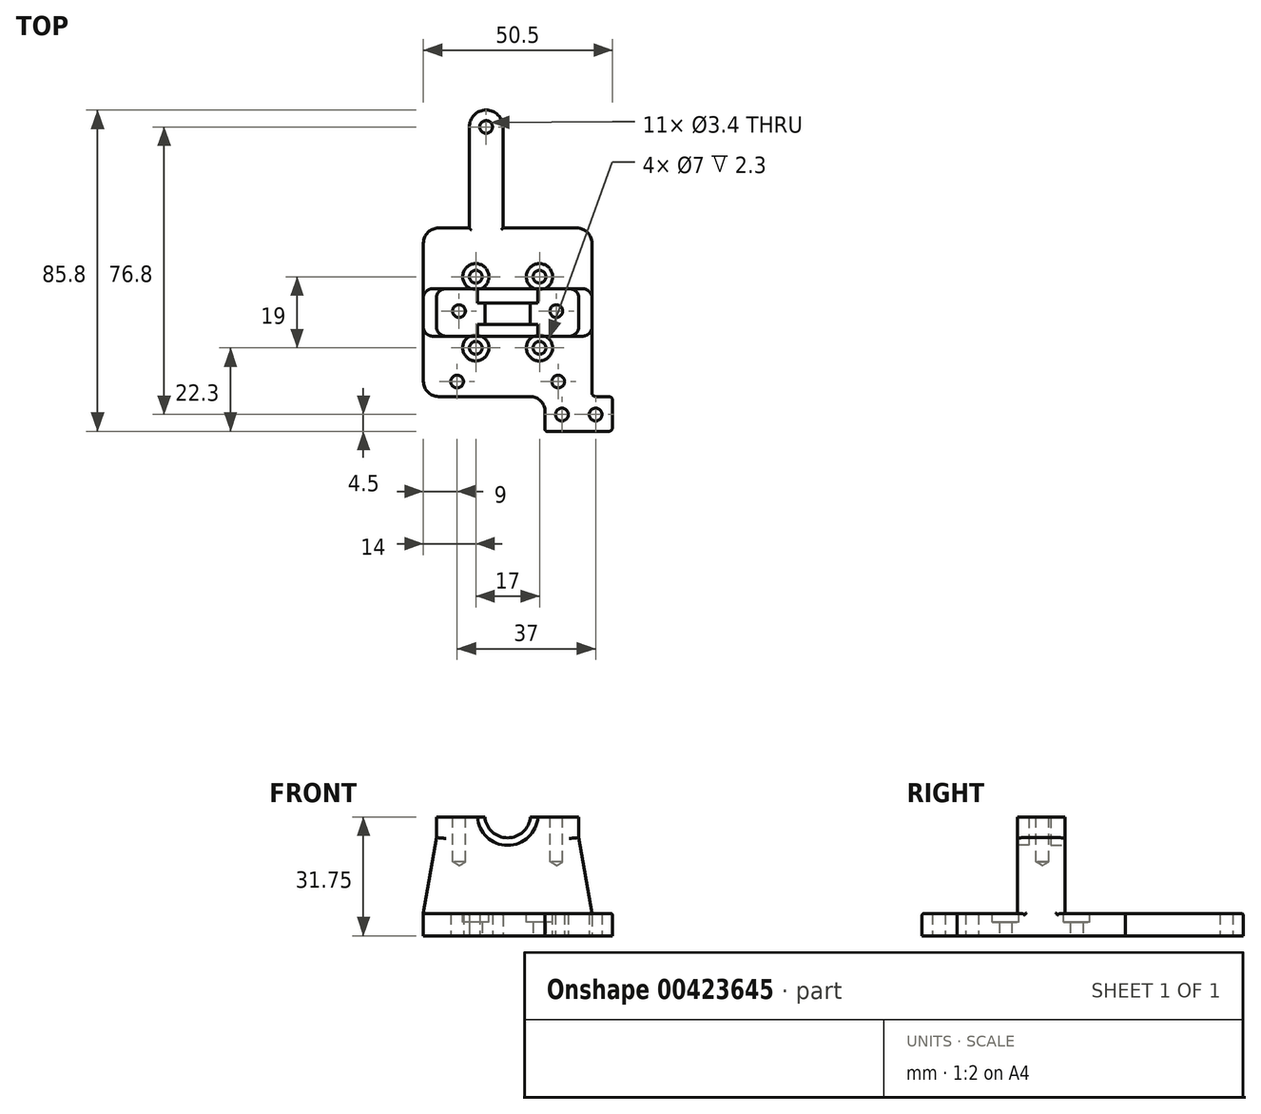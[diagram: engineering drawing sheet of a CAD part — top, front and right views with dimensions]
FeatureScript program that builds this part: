
annotation { "Feature Type Name" : "Feature", "Feature Type Description" : "" }
export const myFeature = defineFeature(function(context is Context, id is Id, definition is map)
    precondition{}
    {
        {
            var Q0;
            Q0=qCreatedBy(makeId("Top.planeOp"),FACE);
            cPlane(context, id + "F0", {"entities" : qUnion([Q0]), "cplaneType" : CPlaneType.OFFSET, "offset" : 16 * mm, "oppositeDirection" : true, "width" : 150 * mm, "height" : 150 * mm});
        }
        {
            var Q0;
            Q0=qCreatedBy(id+"F0.planeOp",FACE);
            var sketch = newSketch(context, id + "F1", { "sketchPlane" : qUnion([Q0])});
            skLineSegment(sketch, "E0.bottom", {"start": v(-22.5, -29.62) * mm, "end": v(-22.5, 7.38) * mm});
            skLineSegment(sketch, "E0.top", {"start": v(22.5, -32.62) * mm, "end": v(22.5, 7.38) * mm});
            skLineSegment(sketch, "E0.left", {"start": v(-18.5, -33.62) * mm, "end": v(6, -33.62) * mm});
            skLineSegment(sketch, "E0.right", {"start": v(-18.5, 11.38) * mm, "end": v(18.5, 11.38) * mm});
            skPoint(sketch, "E1.visualSharp", {"position": v(22.5, -33.62) * mm});
            skPoint(sketch, "E2.visualSharp", {"position": v(22.5, 11.38) * mm});
            skArc(sketch, "E2.filletArc", {"start": v(22.5, 7.38) * mm, "mid": v(21.33, 10.2) * mm, "end": v(18.5, 11.38) * mm});
            skPoint(sketch, "E3.visualSharp", {"position": v(-22.5, 11.38) * mm});
            skArc(sketch, "E3.filletArc", {"start": v(-18.5, 11.38) * mm, "mid": v(-21.33, 10.2) * mm, "end": v(-22.5, 7.38) * mm});
            skPoint(sketch, "E4.visualSharp", {"position": v(-22.5, -33.62) * mm});
            skArc(sketch, "E4.filletArc", {"start": v(-22.5, -29.62) * mm, "mid": v(-21.33, -32.45) * mm, "end": v(-18.5, -33.62) * mm});
            skLineSegment(sketch, "E5.top", {"start": v(22, -42.92) * mm, "end": v(10.5, -42.92) * mm});
            skLineSegment(sketch, "E5.right", {"start": v(10, -37.62) * mm, "end": v(10, -42.42) * mm});
            skPoint(sketch, "E6.visualSharp", {"position": v(10, -42.92) * mm});
            skArc(sketch, "E6.filletArc", {"start": v(10, -42.42) * mm, "mid": v(10.15, -42.77) * mm, "end": v(10.5, -42.92) * mm});
            skPoint(sketch, "E7.visualSharp", {"position": v(22.5, -42.92) * mm});
            skCircle(sketch, "E8", {"center": v(13.5, -29.62) * mm, "radius": 1.7 * mm});
            skPoint(sketch, "E8.first.point", {"position": v(11.95, -30.32) * mm});
            skPoint(sketch, "E8.second.point", {"position": v(15.02, -28.87) * mm});
            skPoint(sketch, "E8.third.point", {"position": v(14.54, -30.97) * mm});
            skLineSegment(sketch, "E9", {"start": v(10, -33.62) * mm, "end": v(22.5, -33.62) * mm, "construction": true});
            skCircle(sketch, "E10.MirrorC", {"center": v(14.5, -38.42) * mm, "radius": 1.7 * mm});
            skLineSegment(sketch, "E11", {"start": v(0, -37.3) * mm, "end": v(0, 46.97) * mm, "construction": true});
            skCircle(sketch, "E12.MirrorC", {"center": v(-13.5, -29.62) * mm, "radius": 1.7 * mm});
            skLineSegment(sketch, "E13", {"start": v(-41.46, -11.12) * mm, "end": v(34.1, -11.12) * mm, "construction": true});
            skCircle(sketch, "E14", {"center": v(-8.5, -20.62) * mm, "radius": 1.7 * mm});
            skCircle(sketch, "E15.MirrorC", {"center": v(8.5, -20.62) * mm, "radius": 1.7 * mm});
            skCircle(sketch, "E16.MirrorC", {"center": v(-8.5, -1.62) * mm, "radius": 1.7 * mm});
            skCircle(sketch, "E17.MirrorC", {"center": v(8.5, -1.62) * mm, "radius": 1.7 * mm});
            skLineSegment(sketch, "E18.bottom", {"start": v(-10.25, 11.38) * mm, "end": v(-1.25, 11.38) * mm});
            skLineSegment(sketch, "E18.left", {"start": v(-10.25, 11.38) * mm, "end": v(-10.25, 38.38) * mm});
            skLineSegment(sketch, "E18.right", {"start": v(-1.25, 11.38) * mm, "end": v(-1.25, 38.38) * mm});
            skArc(sketch, "E19", {"start": v(-10.25, 38.38) * mm, "mid": v(-5.75, 42.88) * mm, "end": v(-1.25, 38.38) * mm});
            skCircle(sketch, "E20", {"center": v(-5.75, 38.38) * mm, "radius": 1.7 * mm});
            skPoint(sketch, "E21.visualSharp", {"position": v(10, -33.62) * mm});
            skArc(sketch, "E21.filletArc", {"start": v(10, -37.62) * mm, "mid": v(8.83, -34.8) * mm, "end": v(6, -33.62) * mm});
            skLineSegment(sketch, "E22", {"start": v(10.13, -20.12) * mm, "end": v(10.13, -52.89) * mm, "construction": true});
            skLineSegment(sketch, "E23", {"start": v(17.44, -42.92) * mm, "end": v(27, -42.92) * mm});
            skLineSegment(sketch, "E24", {"start": v(28, -41.92) * mm, "end": v(28, -34.62) * mm});
            skLineSegment(sketch, "E25", {"start": v(27, -33.62) * mm, "end": v(23.5, -33.62) * mm});
            skPoint(sketch, "E26.visualSharp", {"position": v(28, -42.92) * mm});
            skArc(sketch, "E26.filletArc", {"start": v(27, -42.92) * mm, "mid": v(27.7, -42.63) * mm, "end": v(28, -41.92) * mm});
            skPoint(sketch, "E27.visualSharp", {"position": v(28, -33.62) * mm});
            skArc(sketch, "E27.filletArc", {"start": v(28, -34.62) * mm, "mid": v(27.7, -33.91) * mm, "end": v(27, -33.62) * mm});
            skArc(sketch, "E28.filletArc", {"start": v(22.5, -32.62) * mm, "mid": v(22.8, -33.33) * mm, "end": v(23.5, -33.62) * mm});
            skLineSegment(sketch, "E29", {"start": v(19, -42.92) * mm, "end": v(19, -32.16) * mm, "construction": true});
            skCircle(sketch, "E30.MirrorC", {"center": v(23.5, -38.42) * mm, "radius": 1.7 * mm});
            skLineSegment(sketch, "E31", {"start": v(14.5, -34.27) * mm, "end": v(14.5, -44.4) * mm, "construction": true});
            skSolve(sketch);
        }
        {
            var Q0;
            Q0=qSketchRegion(id+"F1",true);
            extrude(context, id + "F2", {"entities" : qUnion([Q0]), "depth" : 6 * mm});
        }
        {
            var Q0;
            Q0=makeQuery(id+"F2.opExtrude","CAP_FACE",FACE,{"disambiguationData":[OSD([sQuery(id+"F1.wireOp",EDGE,"E0.bottom"),sQuery(id+"F1.wireOp",EDGE,"E0.top"),sQuery(id+"F1.wireOp",EDGE,"E0.left"),sQuery(id+"F1.wireOp",EDGE,"E0.right"),sQuery(id+"F1.wireOp",EDGE,"E2.filletArc"),sQuery(id+"F1.wireOp",EDGE,"E3.filletArc"),sQuery(id+"F1.wireOp",EDGE,"E4.filletArc"),sQuery(id+"F1.wireOp",EDGE,"E5.top"),sQuery(id+"F1.wireOp",EDGE,"E5.left"),sQuery(id+"F1.wireOp",EDGE,"E5.right"),sQuery(id+"F1.wireOp",EDGE,"E6.filletArc"),sQuery(id+"F1.wireOp",EDGE,"E7.filletArc"),sQuery(id+"F1.wireOp",EDGE,"E8"),sQuery(id+"F1.wireOp",EDGE,"E10.MirrorC"),sQuery(id+"F1.wireOp",EDGE,"E12.MirrorC"),sQuery(id+"F1.wireOp",EDGE,"1abc18dc-51f7-492f-8969-0957bb5dfce40.MirrorC"),sQuery(id+"F1.wireOp",EDGE,"E14"),sQuery(id+"F1.wireOp",EDGE,"E15.MirrorC"),sQuery(id+"F1.wireOp",EDGE,"E16.MirrorC"),sQuery(id+"F1.wireOp",EDGE,"E17.MirrorC"),sQuery(id+"F1.wireOp",EDGE,"E18.left"),sQuery(id+"F1.wireOp",EDGE,"E18.right"),sQuery(id+"F1.wireOp",EDGE,"E19"),sQuery(id+"F1.wireOp",EDGE,"E20")])],"isStart":false});
            var sketch = newSketch(context, id + "F3", { "sketchPlane" : qUnion([Q0])});
            skPoint(sketch, "E32.0", {"position": v(-8.5, -1.62) * mm});
            skPoint(sketch, "E33.0", {"position": v(8.5, -1.62) * mm});
            skPoint(sketch, "E34.0", {"position": v(-8.5, -20.62) * mm});
            skPoint(sketch, "E35.0", {"position": v(8.5, -20.62) * mm});
            skSolve(sketch);
        }
        {
            var Q0;
            Q0=sQuery(id+"F3.wireOp",VERTEX,"E32.0");
            var Q1;
            Q1=sQuery(id+"F3.wireOp",VERTEX,"E33.0");
            var Q2;
            Q2=sQuery(id+"F3.wireOp",VERTEX,"E34.0");
            var Q3;
            Q3=sQuery(id+"F3.wireOp",VERTEX,"E35.0");
            var Q4;
            Q4=makeQuery(id+"F2.opExtrude","SWEPT_BODY",BODY,{"disambiguationData":[OSD([sQuery(id+"F1.wireOp",EDGE,"E0.bottom"),sQuery(id+"F1.wireOp",EDGE,"E0.top"),sQuery(id+"F1.wireOp",EDGE,"E0.left"),sQuery(id+"F1.wireOp",EDGE,"E0.right"),sQuery(id+"F1.wireOp",EDGE,"E2.filletArc"),sQuery(id+"F1.wireOp",EDGE,"E3.filletArc"),sQuery(id+"F1.wireOp",EDGE,"E4.filletArc"),sQuery(id+"F1.wireOp",EDGE,"E5.top"),sQuery(id+"F1.wireOp",EDGE,"E5.left"),sQuery(id+"F1.wireOp",EDGE,"E5.right"),sQuery(id+"F1.wireOp",EDGE,"E6.filletArc"),sQuery(id+"F1.wireOp",EDGE,"E7.filletArc"),sQuery(id+"F1.wireOp",EDGE,"E8"),sQuery(id+"F1.wireOp",EDGE,"E10.MirrorC"),sQuery(id+"F1.wireOp",EDGE,"E12.MirrorC"),sQuery(id+"F1.wireOp",EDGE,"1abc18dc-51f7-492f-8969-0957bb5dfce40.MirrorC"),sQuery(id+"F1.wireOp",EDGE,"E14"),sQuery(id+"F1.wireOp",EDGE,"E15.MirrorC"),sQuery(id+"F1.wireOp",EDGE,"E16.MirrorC"),sQuery(id+"F1.wireOp",EDGE,"E17.MirrorC"),sQuery(id+"F1.wireOp",EDGE,"E18.left"),sQuery(id+"F1.wireOp",EDGE,"E18.right"),sQuery(id+"F1.wireOp",EDGE,"E19"),sQuery(id+"F1.wireOp",EDGE,"E20")])]});
            hole(context, id + "F4", {"style" : HoleStyle.C_BORE, "endStyle" : HoleEndStyle.THROUGH, "holeDiameter" : 3.4 * mm, "cBoreDiameter" : 7 * mm, "cBoreDepth" : 2.3 * mm, "tappedDepth" : 12 * mm, "tapClearance" : 3, "startFromSketch" : true, "locations" : qUnion([Q0, Q1, Q2, Q3]), "scope" : qUnion([Q4])});
        }
        {
            var Q0;
            Q0=qCreatedBy(makeId("Front.planeOp"),FACE);
            cPlane(context, id + "F5", {"entities" : qUnion([Q0]), "cplaneType" : CPlaneType.OFFSET, "offset" : 4.8 * mm, "width" : 150 * mm, "height" : 150 * mm});
        }
        {
            var Q0;
            Q0=qCreatedBy(id+"F5.planeOp",FACE);
            var sketch = newSketch(context, id + "F6", { "sketchPlane" : qUnion([Q0])});
            skLineSegment(sketch, "E36", {"start": v(27.9, -10) * mm, "end": v(9.75, -10) * mm, "construction": true});
            skLineSegment(sketch, "E37.bottom", {"start": v(22.5, -10) * mm, "end": v(9.75, -10) * mm});
            skLineSegment(sketch, "E37.top", {"start": v(19, 15.75) * mm, "end": v(6.08, 15.75) * mm});
            skLineSegment(sketch, "E38", {"start": v(0, -27.94) * mm, "end": v(0, 48.8) * mm, "construction": true});
            skLineSegment(sketch, "E39.MirrorCS", {"start": v(1.25, -10) * mm, "end": v(-18.5, -10) * mm, "construction": true});
            skLineSegment(sketch, "E40", {"start": v(19, 15.75) * mm, "end": v(19, 10.25) * mm});
            skLineSegment(sketch, "E41", {"start": v(22.5, -10) * mm, "end": v(19, 10.25) * mm});
            skLineSegment(sketch, "E42.MirrorCS", {"start": v(-19, 15.75) * mm, "end": v(-19, 10.25) * mm});
            skLineSegment(sketch, "E43.MirrorCS", {"start": v(-22.5, -10) * mm, "end": v(-19, 10.25) * mm});
            skArc(sketch, "E44", {"start": v(-6.08, 15.75) * mm, "mid": v(0, 10.19) * mm, "end": v(6.08, 15.75) * mm});
            skLineSegment(sketch, "E45.trimOffspring", {"start": v(-6.08, 15.75) * mm, "end": v(-19, 15.75) * mm});
            skPoint(sketch, "E46.orphan", {"position": v(18.5, -10) * mm});
            skLineSegment(sketch, "E47.trimOffspring", {"start": v(-9.75, -10) * mm, "end": v(-22.5, -10) * mm});
            skPoint(sketch, "E48.orphan", {"position": v(-1.25, -10) * mm});
            skLineSegment(sketch, "E49.trimOffspring", {"start": v(-1.25, -10) * mm, "end": v(-28.56, -10) * mm, "construction": true});
            skPoint(sketch, "E50.orphan", {"position": v(0, -10) * mm});
            skLineSegment(sketch, "E51", {"start": v(-9.75, -10) * mm, "end": v(9.75, -10) * mm});
            skSolve(sketch);
        }
        {
            var Q0;
            Q0=qSketchRegion(id+"F6",true);
            extrude(context, id + "F7", {"entities" : qUnion([Q0]), "operationType" : NewBodyOperationType.ADD, "depth" : 12.7 * mm});
        }
        {
            var Q0;
            Q0=makeQuery(id+"F7.opExtrude","CAP_EDGE",EDGE,{"disambiguationData":[OSD([sQuery(id+"F6.wireOp",EDGE,"E41")])],"isStart":false});
            var Q1;
            Q1=makeQuery(id+"F7.opExtrude","CAP_EDGE",EDGE,{"disambiguationData":[OSD([sQuery(id+"F6.wireOp",EDGE,"E40")])],"isStart":false});
            var Q2;
            Q2=makeQuery(id+"F7.opExtrude","CAP_EDGE",EDGE,{"disambiguationData":[OSD([sQuery(id+"F6.wireOp",EDGE,"E41")])],"isStart":true});
            var Q3;
            Q3=makeQuery(id+"F7.opExtrude","CAP_EDGE",EDGE,{"disambiguationData":[OSD([sQuery(id+"F6.wireOp",EDGE,"E40")])],"isStart":true});
            var Q4;
            Q4=makeQuery(id+"F7.opExtrude","CAP_EDGE",EDGE,{"disambiguationData":[OSD([sQuery(id+"F6.wireOp",EDGE,"E43.MirrorCS")])],"isStart":true});
            var Q5;
            Q5=makeQuery(id+"F7.opExtrude","CAP_EDGE",EDGE,{"disambiguationData":[OSD([sQuery(id+"F6.wireOp",EDGE,"E42.MirrorCS")])],"isStart":true});
            var Q6;
            Q6=makeQuery(id+"F7.opExtrude","CAP_EDGE",EDGE,{"disambiguationData":[OSD([sQuery(id+"F6.wireOp",EDGE,"E43.MirrorCS")])],"isStart":false});
            var Q7;
            Q7=makeQuery(id+"F7.opExtrude","CAP_EDGE",EDGE,{"disambiguationData":[OSD([sQuery(id+"F6.wireOp",EDGE,"E42.MirrorCS")])],"isStart":false});
            fillet(context, id + "F8", {"entities" : qUnion([Q0, Q1, Q2, Q3, Q4, Q5, Q6, Q7]), "radius" : 2.5 * mm, "tangentPropagation" : true, "allowEdgeOverflow" : false});
        }
        {
            var Q0;
            {var subQ0=sQuery(id+"F6.wireOp",EDGE,"E41");var subQ1=sQuery(id+"F6.wireOp",EDGE,"E37.bottom");var subQ2=sQuery(id+"F1.wireOp",EDGE,"E7.filletArc");var subQ3=sQuery(id+"F1.wireOp",EDGE,"E5.left");var subQ4=sQuery(id+"F1.wireOp",EDGE,"E0.top");var subQ5=makeQuery(id+"F2.opExtrude","CAP_EDGE",EDGE,{"disambiguationData":[OSD([subQ4,subQ3])],"isStart":false});Q0=makeQuery(id+"F8.opFillet","MERGE",EDGE,{"derivedFrom":[makeQuery(id+"F7.boolean.opBoolean","MERGE",EDGE,{"derivedFrom":[subQ5,makeQuery(id+"F7.opExtrude","SWEPT_EDGE",EDGE,{"disambiguationData":[OSD([subQ1,subQ0])]})]}),makeQuery(id+"F7.boolean.opBoolean","SPLIT",EDGE,{"disambiguationData":[TD([makeQuery(id+"F2.opExtrude","SWEPT_FACE",FACE,{"disambiguationData":[OSD([subQ2])]})])],"derivedFrom":subQ5})]});}
            var Q1;
            {var subQ0=sQuery(id+"F6.wireOp",EDGE,"E41");var subQ1=sQuery(id+"F6.wireOp",EDGE,"E37.bottom");var subQ2=sQuery(id+"F1.wireOp",EDGE,"E5.left");var subQ3=sQuery(id+"F1.wireOp",EDGE,"E0.top");var subQ4=sQuery(id+"F1.wireOp",EDGE,"E2.filletArc");var subQ5=makeQuery(id+"F2.opExtrude","CAP_EDGE",EDGE,{"disambiguationData":[OSD([subQ3,subQ2])],"isStart":false});Q1=makeQuery(id+"F8.opFillet","MERGE",EDGE,{"derivedFrom":[makeQuery(id+"F7.boolean.opBoolean","MERGE",EDGE,{"derivedFrom":[subQ5,makeQuery(id+"F7.opExtrude","SWEPT_EDGE",EDGE,{"disambiguationData":[OSD([subQ1,subQ0])]})]}),makeQuery(id+"F7.boolean.opBoolean","SPLIT",EDGE,{"disambiguationData":[TD([makeQuery(id+"F2.opExtrude","SWEPT_FACE",FACE,{"disambiguationData":[OSD([subQ4])]})])],"derivedFrom":subQ5})]});}
            var Q2;
            Q2=makeQuery(id+"F2.opExtrude","CAP_EDGE",EDGE,{"disambiguationData":[OSD([sQuery(id+"F1.wireOp",EDGE,"E0.left")])],"isStart":false});
            var Q3;
            Q3=makeQuery(id+"F2.opExtrude","CAP_EDGE",EDGE,{"disambiguationData":[OSD([sQuery(id+"F1.wireOp",EDGE,"E4.filletArc")])],"isStart":false});
            var Q4;
            {var subQ0=sQuery(id+"F6.wireOp",EDGE,"E47.trimOffspring");var subQ1=sQuery(id+"F6.wireOp",EDGE,"E43.MirrorCS");var subQ2=sQuery(id+"F1.wireOp",EDGE,"E3.filletArc");var subQ3=sQuery(id+"F1.wireOp",EDGE,"E0.bottom");var subQ4=makeQuery(id+"F2.opExtrude","CAP_EDGE",EDGE,{"disambiguationData":[OSD([subQ3])],"isStart":false});Q4=makeQuery(id+"F8.opFillet","MERGE",EDGE,{"derivedFrom":[makeQuery(id+"F7.boolean.opBoolean","MERGE",EDGE,{"derivedFrom":[subQ4,makeQuery(id+"F7.opExtrude","SWEPT_EDGE",EDGE,{"disambiguationData":[OSD([subQ1,subQ0])]})]}),makeQuery(id+"F7.boolean.opBoolean","SPLIT",EDGE,{"disambiguationData":[TD([makeQuery(id+"F2.opExtrude","SWEPT_FACE",FACE,{"disambiguationData":[OSD([subQ2])]})])],"derivedFrom":subQ4})]});}
            var Q5;
            Q5=makeQuery(id+"F2.opExtrude","CAP_EDGE",EDGE,{"disambiguationData":[OSD([sQuery(id+"F1.wireOp",EDGE,"E18.left")])],"isStart":false});
            var Q6;
            Q6=makeQuery(id+"F2.opExtrude","CAP_EDGE",EDGE,{"disambiguationData":[OSD([sQuery(id+"F1.wireOp",EDGE,"E18.right")])],"isStart":false});
            var Q7;
            Q7=makeQuery(id+"F7.opExtrude","CAP_EDGE",EDGE,{"disambiguationData":[OSD([sQuery(id+"F6.wireOp",EDGE,"3a945508-988b-4af8-a3a7-beca160494270.MirrorCS")])],"isStart":true});
            var Q8;
            Q8=makeQuery(id+"F7.opExtrude","CAP_EDGE",EDGE,{"disambiguationData":[OSD([sQuery(id+"F6.wireOp",EDGE,"a3d874f1-bc51-495c-9086-fb889d6b969a.right")])],"isStart":true});
            var Q9;
            Q9=makeQuery(id+"F7.opExtrude","CAP_EDGE",EDGE,{"disambiguationData":[OSD([sQuery(id+"F6.wireOp",EDGE,"a3d874f1-bc51-495c-9086-fb889d6b969a.top"),sQuery(id+"F6.wireOp",EDGE,"b65f0abd-e565-49f9-979e-a5ecc3f08d520.MirrorCS")])],"isStart":true});
            var Q10;
            Q10=makeQuery(id+"F7.opExtrude","CAP_EDGE",EDGE,{"disambiguationData":[OSD([sQuery(id+"F6.wireOp",EDGE,"3a945508-988b-4af8-a3a7-beca160494270.MirrorCS")])],"isStart":false});
            var Q11;
            Q11=makeQuery(id+"F7.opExtrude","CAP_EDGE",EDGE,{"disambiguationData":[OSD([sQuery(id+"F6.wireOp",EDGE,"a3d874f1-bc51-495c-9086-fb889d6b969a.top"),sQuery(id+"F6.wireOp",EDGE,"b65f0abd-e565-49f9-979e-a5ecc3f08d520.MirrorCS")])],"isStart":false});
            var Q12;
            Q12=makeQuery(id+"F7.opExtrude","CAP_EDGE",EDGE,{"disambiguationData":[OSD([sQuery(id+"F6.wireOp",EDGE,"a3d874f1-bc51-495c-9086-fb889d6b969a.right")])],"isStart":false});
            fillet(context, id + "F9", {"entities" : qUnion([Q0, Q1, Q2, Q3, Q4, Q5, Q6, Q7, Q8, Q9, Q10, Q11, Q12]), "radius" : 0.5 * mm, "tangentPropagation" : true, "allowEdgeOverflow" : false});
        }
        {
            var Q0;
            Q0=makeQuery(id+"F7.opExtrude","SWEPT_FACE",FACE,{"disambiguationData":[OSD([sQuery(id+"F6.wireOp",EDGE,"E45.trimOffspring")])]});
            var sketch = newSketch(context, id + "F10", { "sketchPlane" : qUnion([Q0])});
            skCircle(sketch, "E52", {"center": v(-13, -10.8) * mm, "radius": 1.65 * mm});
            skLineSegment(sketch, "E53", {"start": v(0, 0) * mm, "end": v(0, -28.18) * mm, "construction": true});
            skCircle(sketch, "E54.MirrorC", {"center": v(13, -10.8) * mm, "radius": 1.65 * mm});
            skSolve(sketch);
        }
        {
            var Q0;
            Q0=sQuery(id+"F10.wireOp",VERTEX,"E52.center");
            var Q1;
            Q1=sQuery(id+"F10.wireOp",VERTEX,"E54.MirrorC.center");
            var Q2;
            Q2=makeQuery(id+"F2.opExtrude","SWEPT_BODY",BODY,{"disambiguationData":[OSD([sQuery(id+"F1.wireOp",EDGE,"E0.bottom"),sQuery(id+"F1.wireOp",EDGE,"E0.top"),sQuery(id+"F1.wireOp",EDGE,"E0.left"),sQuery(id+"F1.wireOp",EDGE,"E0.right"),sQuery(id+"F1.wireOp",EDGE,"E2.filletArc"),sQuery(id+"F1.wireOp",EDGE,"E3.filletArc"),sQuery(id+"F1.wireOp",EDGE,"E4.filletArc"),sQuery(id+"F1.wireOp",EDGE,"E5.top"),sQuery(id+"F1.wireOp",EDGE,"E5.left"),sQuery(id+"F1.wireOp",EDGE,"E5.right"),sQuery(id+"F1.wireOp",EDGE,"E6.filletArc"),sQuery(id+"F1.wireOp",EDGE,"E7.filletArc"),sQuery(id+"F1.wireOp",EDGE,"E8"),sQuery(id+"F1.wireOp",EDGE,"E10.MirrorC"),sQuery(id+"F1.wireOp",EDGE,"E12.MirrorC"),sQuery(id+"F1.wireOp",EDGE,"1abc18dc-51f7-492f-8969-0957bb5dfce40.MirrorC"),sQuery(id+"F1.wireOp",EDGE,"E14"),sQuery(id+"F1.wireOp",EDGE,"E15.MirrorC"),sQuery(id+"F1.wireOp",EDGE,"E16.MirrorC"),sQuery(id+"F1.wireOp",EDGE,"E17.MirrorC"),sQuery(id+"F1.wireOp",EDGE,"E18.left"),sQuery(id+"F1.wireOp",EDGE,"E18.right"),sQuery(id+"F1.wireOp",EDGE,"E19"),sQuery(id+"F1.wireOp",EDGE,"E20")])]});
            hole(context, id + "F11", {"style" : HoleStyle.SIMPLE, "endStyle" : HoleEndStyle.BLIND, "holeDiameter" : 3.4 * mm, "holeDepth" : 12 * mm, "tappedDepth" : 12 * mm, "tapClearance" : 3, "locations" : qUnion([Q0, Q1]), "scope" : qUnion([Q2])});
        }
        {
            var Q0;
            Q0=makeQuery(id+"F7.opExtrude","CAP_FACE",FACE,{"disambiguationData":[OSD([sQuery(id+"F6.wireOp",EDGE,"E37.bottom"),sQuery(id+"F6.wireOp",EDGE,"E37.top"),sQuery(id+"F6.wireOp",EDGE,"a3d874f1-bc51-495c-9086-fb889d6b969a.top"),sQuery(id+"F6.wireOp",EDGE,"a3d874f1-bc51-495c-9086-fb889d6b969a.right"),sQuery(id+"F6.wireOp",EDGE,"b65f0abd-e565-49f9-979e-a5ecc3f08d520.MirrorCS"),sQuery(id+"F6.wireOp",EDGE,"3a945508-988b-4af8-a3a7-beca160494270.MirrorCS"),sQuery(id+"F6.wireOp",EDGE,"E40"),sQuery(id+"F6.wireOp",EDGE,"E41"),sQuery(id+"F6.wireOp",EDGE,"E42.MirrorCS"),sQuery(id+"F6.wireOp",EDGE,"E43.MirrorCS"),sQuery(id+"F6.wireOp",EDGE,"E44"),sQuery(id+"F6.wireOp",EDGE,"E45.trimOffspring"),sQuery(id+"F6.wireOp",EDGE,"E47.trimOffspring")])],"isStart":false});
            var sketch = newSketch(context, id + "F12", { "sketchPlane" : qUnion([Q0])});
            skArc(sketch, "E55.0", {"start": v(-6.08, 15.75) * mm, "mid": v(0, 10.19) * mm, "end": v(6.08, 15.75) * mm});
            skArc(sketch, "E56", {"start": v(-8.08, 15.75) * mm, "mid": v(0, 8.19) * mm, "end": v(8.08, 15.75) * mm});
            skLineSegment(sketch, "E57.0", {"start": v(-6.08, 15.75) * mm, "end": v(-16.5, 15.75) * mm});
            skLineSegment(sketch, "E58.0", {"start": v(16.5, 15.75) * mm, "end": v(6.08, 15.75) * mm});
            skSolve(sketch);
        }
        {
            var Q0;
            Q0=qSketchRegion(id+"F12",true);
            extrude(context, id + "F13", {"entities" : qUnion([Q0]), "operationType" : NewBodyOperationType.REMOVE, "oppositeDirection" : true, "depth" : 3.1 * mm});
        }
        {
            var Q0;
            Q0=makeQuery(id+"F7.opExtrude","CAP_FACE",FACE,{"disambiguationData":[OSD([sQuery(id+"F6.wireOp",EDGE,"E37.bottom"),sQuery(id+"F6.wireOp",EDGE,"E37.top"),sQuery(id+"F6.wireOp",EDGE,"a3d874f1-bc51-495c-9086-fb889d6b969a.top"),sQuery(id+"F6.wireOp",EDGE,"a3d874f1-bc51-495c-9086-fb889d6b969a.right"),sQuery(id+"F6.wireOp",EDGE,"b65f0abd-e565-49f9-979e-a5ecc3f08d520.MirrorCS"),sQuery(id+"F6.wireOp",EDGE,"3a945508-988b-4af8-a3a7-beca160494270.MirrorCS"),sQuery(id+"F6.wireOp",EDGE,"E40"),sQuery(id+"F6.wireOp",EDGE,"E41"),sQuery(id+"F6.wireOp",EDGE,"E42.MirrorCS"),sQuery(id+"F6.wireOp",EDGE,"E43.MirrorCS"),sQuery(id+"F6.wireOp",EDGE,"E44"),sQuery(id+"F6.wireOp",EDGE,"E45.trimOffspring"),sQuery(id+"F6.wireOp",EDGE,"E47.trimOffspring")])],"isStart":true});
            var sketch = newSketch(context, id + "F14", { "sketchPlane" : qUnion([Q0])});
            skArc(sketch, "E59.0", {"start": v(6.08, 15.75) * mm, "mid": v(0, 10.19) * mm, "end": v(-6.08, 15.75) * mm});
            skLineSegment(sketch, "E60.0", {"start": v(6.08, 15.75) * mm, "end": v(16.5, 15.75) * mm});
            skLineSegment(sketch, "E61.0", {"start": v(-16.5, 15.75) * mm, "end": v(-6.08, 15.75) * mm});
            skArc(sketch, "E62.0", {"start": v(8.08, 15.75) * mm, "mid": v(0, 8.19) * mm, "end": v(-8.08, 15.75) * mm});
            skSolve(sketch);
        }
        {
            var Q0;
            {var subQ0=sQuery(id+"F14.wireOp",EDGE,"E59.0");Q0=makeQuery(id+"F14.imprint","IMPRINT",FACE,{"disambiguationData":[TD([[makeQuery(id+"F14.imprint","IMPRINT",EDGE,{"derivedFrom":subQ0}),1.0]])]});}
            extrude(context, id + "F15", {"entities" : qUnion([Q0]), "operationType" : NewBodyOperationType.REMOVE, "oppositeDirection" : true, "depth" : 3.8 * mm});
        }
    });
